# Revit family: Furniture_GroheLimited_Essentials_ToiletPaperHolder_40689001_METRIC
name_source: partatom
category: Furniture
revit_build: Autodesk Revit 2015 (Build: 20160512_1515(x64)
units: mm (PartAtom-declared; Revit-internal decimal feet)

## types (9) — shared parameters
ADACompliant = No
Assembly Code = D2010
AssetType = Fixed
BIMObjectName = Furniture_GroheLimited_Essentials_ToiletPaperHolder_40689001_METRIC
CW Connection = No
CWFU = 4.5
ClassificationName = Uniclass2015
ClassificationValue = Pr_40_20_76_88
ColdWaterConnectionDiameter = 10 mm  [stored 0.0328084 ft]
Description = Essentials Toilet paper holder material: metal without cover concealed fastening GROHE StarLight chrome finish
DurationUnit = Years
Ecojoy = No
Features = Essentials Toilet paper holder material: metal without cover concealed fastening GROHE StarLight chrome finish
HW Connection = No
HWFU = 4.5
HotWaterConnectionDiameter = 10 mm  [stored 0.0328084 ft]
IfcExportAs = IfcPipeFitting
IfcExportType = IfcPipeFittingType
Keynote = N13
LowEmittingMaterial = No
Manufacturer = Grohe Limited
ManufacturerName = Grohe Limited
MasterformatNumber = 01 52 19
MasterformatTitle = Sanitary Facilities
Model = Essentials Toilet paper holder
ModelReference = Essentials Toilet paper holder
NBSDescription = Toilet roll holders
NBSObjectName = Grohe Limited - Toilet roll holders
NBSReference = 45-35-72/368
NominalDepth = 44 mm  [stored 0.144357 ft]
NominalHeight = 119 mm  [stored 0.39042 ft]
NominalLength = 54 mm  [stored 0.177165 ft]
PipeMaterial = GroheLimited-Pipework
ProductDocumentationLink = https://cdn.cloud.grohe.com
ProductPageURL = https://www.grohe.co.uk
ProductionYear = 2017
ToiletPaper = Grohe-Toilet Paper
TypeName = Essentials Toilet paper holder
URL = www.grohe.com
Vent Connection = No
WarrantyDurationUnit = Years
Waste Connection = No
_BSBibleVersion = 14
_CurrentRevision = 1
_DistributedBy = www.bimstore.co.uk
zero-valued in all types: Cost, Default Elevation, ExpectedLife, WFU, _BimSpecGuid

## per-type parameters (varying)
| type | Color | Finish | Material | PrimaryMaterial |
| 40689001 | Chrome | Chrome | Chrome | GroheLimited-Chrome |
| 40689DA1 | Warm Sunset | Warm Sunset | Warm Sunset | GroheLimited-WarmSunset |
| 40689GL1 | Cool Sunrise | Cool Sunrise | Cool Sunrise | GroheLimited-CoolSunrise |
| 40689GN1 | Brushed Cool Sunrise | Brushed Cool Sunrise | Brushed Cool Sunrise | GroheLimited-BrushedCoolSunrise |
| 40689DL1 | Brushed Warm Sunset | Brushed Warm Sunset | Brushed Warm Sunset | GroheLimited-BrushedWarmSunset |
| 40689A01 | Hard Graphite | Hard Graphite | Hard Graphite | GroheLimited-HardGraphite |
| 40689AL1 | Brushed Hard Graphite | Brushed Hard Graphite | Brushed Hard Graphite | GroheLimited-BrushedHardGraphite |
| 40689BE1 | Polished Nickel | Polished Nickel | Polished Nickel | GroheLimited-Nickel |
| 40689EN1 | Brushed Nickel | Brushed Nickel | Brushed Nickel | GroheLimited-BrushedNickel |

note: column(s) folded — value = type name in every type: ModelNumber, Type Comments

note: [stored X ft] marks values corroborated as IEEE doubles in the binary element streams (Revit-internal decimal feet)

## geometry (parser evidence)
native form markers: Blend x6, Sweep x3
no freeform markers — native parametric forms only
